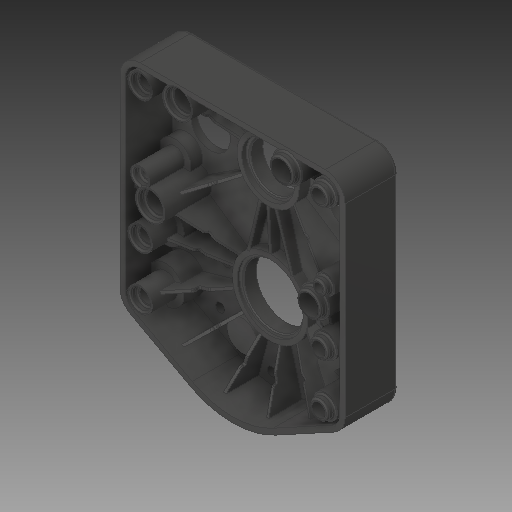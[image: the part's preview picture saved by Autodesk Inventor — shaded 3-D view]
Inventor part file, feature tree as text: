
AUTODESK INVENTOR PART (.ipt)
format: ipt  version: 2017 (Build 210142000, 142)  size: 863,744 bytes
history: native  units: in
note: dims shown in document units (in); Inventor stores cm internally (conversion verified against a paired STEP export)
features: fillet x1
ambient origin geometry x8: Origin, YZ Plane, XZ Plane, XY Plane, X Axis, Y Axis, Z Axis, Center Point
bodies: Solid1 (feature_tree)
feature tree (1):
  fillet  "Fillet18"  [1 undecoded]
note: 1 required parameter value undecoded (feature->parameter linkage not recoverable at this tier; creation-order binding heuristic only, values carry confidence <= 0.55)
